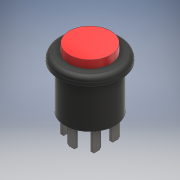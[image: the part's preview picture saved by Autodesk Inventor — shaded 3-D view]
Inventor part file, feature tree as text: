
AUTODESK INVENTOR PART (.ipt)
format: ipt  version: 2018 (Build 220112000, 112)  size: 206,336 bytes
history: native  units: mm
features: extrude x4, sketch x4, other x1, fillet x1, chamfer x1
ambient origin geometry x8: Origin, YZ Plane, XZ Plane, XY Plane, X Axis, Y Axis, Z Axis, Center Point
bodies: Body1 (feature_tree)
feature tree (11):
  other  "ソリッド1"
  extrude  "押し出し1"  Depth=16.0mm
  extrude  "押し出し2"  Depth=14.0mm TaperAngle=0.0deg
  fillet  "フィレット1"  Radius=20.0mm
  extrude  "押し出し3"  Depth=2.5mm TaperAngle=0.0deg
  extrude  "押し出し4"  Depth=1.5mm
  chamfer  "面取り1"  Distance=13.33mm
  sketch  "スケッチ1"
  sketch  "スケッチ2"
  sketch  "スケッチ3"
  sketch  "スケッチ4"
